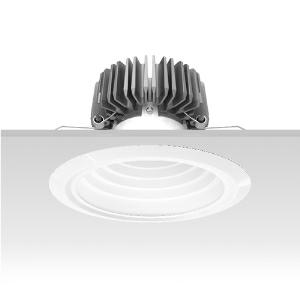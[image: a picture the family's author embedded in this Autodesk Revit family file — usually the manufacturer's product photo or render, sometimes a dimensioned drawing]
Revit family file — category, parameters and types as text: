
# Revit family: 3f_filippi_-_3f_reno_bianco_ampio_3f_filippi_-_30687_a01025_-_3f_reno_200_wh_4000-840_dali_wide___vt_wh_5cad
name_source: partatom
category: Lighting Fixtures
units: mm (PartAtom-declared; Revit-internal decimal feet)

## family parameters
Cut with Voids When Loaded = No
Host = Face
Light Source = No
Part Type = Normal
Room Calculation Point = No
Round Connector Dimension = Use Diameter
Shared = No

## types (1)
- 3F Filippi - 3F Reno Bianco Ampio (1 x LED, 3379 lm, 36 W, 4000 K)
    Apparent Load = 36 VA
    Approval mark = CE
    CIE Flux Codes = 75 94 99 100 100
    Color Rendering = 80
    Color Temperature = 4000 K
    Control Gear = Electronic transformer
    Default Elevation = 1800 mm
    Description = ILLUMINOTECHNICAL
Luminous efficiency 100% (DLOR 100%, ULOR 0%).
Initial luminous flux of the luminaire 3379 lm.
Direct symmetric wide distribution.
Installation Interdistance Transv.D = 1.56 x hu - Long.D = 1.56 x hu.
Tabular UGR (CIE 117 - 4H-8H; S=0.25H; 70/50/20): RUG 22.8 - 22.7.
Beam angle: 74° - 74°.
Luminous efficacy 94 lm/W.
Lifetime (L90/B10): 30000 h. (tq+25°C)
Lifetime (L85/B10): 50000 h. (tq+25°C)
Lifetime (L70/B10): 80000 h. (tq+25°C)
Sudden decreased luminous flux after 50000 hours: 0% (C0).
Photobiological safety in compliance with IEC/TR 62778: RG1 low risk, (IEC 62471).
In compliance with IEC/EN 62722-2-1 - IEC/EN 62717 standards.

SOURCE
Compact LED module 4000/840.
Energy efficiency class (UE 2019/2020 - UE 2019/2015): D.
CIE 13.3 Colour rendering index: CRI >80 (R9 <50%).
IES TM-30 Fidelity Index: Rf = 84 Rg = 95.
CCT nominal colour temperature 4000 K.
Colour initial tolerance (MacAdam): SDCM 3.
Zhaga Book 3 compliant.

MECHANICAL
Passive heat dissipator in die-casting aluminium, oversized, for optimum thermal management of the LED module.
Parabolic element with graduated/concentric rings in white polycarbonate.
Transparent external lens with glossy and satin differentiated surfaces, with a cooling and anti-insect system in methacrylate (PMMA).
Fastening spring clips in stainless steel.
Dimensions: diameter 226 mm, height 146 mm. Weight 1.76 kg.
IP44 protection degree for exposed part, IP20 for recessed part.
Mechanical strength to impacts IK06 (1 joule).
Glow-wire test resistance 650°C.

ELECTRICAL
Wiring on a separate unit.
Halogen Free DALI-2 DATI (Parts 251, 252, 253), PUSH-DIM, electronic wiring 230V-50/60Hz, power factor 0.97 at full load, THD <25%, constant output current, SELV, class II, 1 driver, 1 DALI addresse.
Power of the luminaire 36 W.
ENEC - CE.
SAFE FLICKER: PstLM=<1 and SVM=<0.4 (IEC TR 61547-1 and IEC TR 63158), to ensure a more comfortable and safe light.
Luminaire compliant with EN 60598-2-22 for power supply from a centralised emergency system CPSS (Central Power Supply System), not incorporated in the luminaire - high risk areas excluded. The default power and flux are 100% in AC and 100% in DC.
Ambient temperature from 0°C to +25°C.
Temperature class T6 max 85°C.
Relative humidity UR: <85%.

INSTALLATION
Pull-up recessed fitting.
False ceiling carving: 200 mm.
All accessories dedicated to this product are available on the Catalog and on our website www.3F-Filippi.com.

ACCESSORIES
A01025 - VT transparent glass, tempered, not flammable, locked and in line with the trim, in white polycarbonate.

APPLICATIONS
Environments: architectural, commercial, exhibition areas, transit areas, corridors, shops, display windows, service areas.
In false ceilings with narrow voids.

LIGHT MANAGEMENT
Recommended minimum setting: 10%.
The luminaire, equipped with (DALI-2 DATI) driver, can be controlled manually with 3F Easy Dim technology or automatically/manually with wired or wireless DALI/D2D control systems.
The D2D driver guarantees interoperability with other devices with the same certification by making the following information available:
Device Data (Part 251), Energy Report (Part 252), Diagnosis & Maintenance (Part 253).
In electrical systems without a regulation system (manual or automatic) and DALI bus, a suitable jumper must be made on the DA-DA terminals of the appliance.

WARNING
Luminaire designed for disposal/recycling at end-of-life.
Replaceable (LED only) light source by a professional. Replaceable control gear by a professional.
    Height = 0 mm  [stored 0 ft]
    Lamp = 1 x LED
    Lamp Light Flux = 3379 lm
    Lamp Power = 36 W
    Lamp count = 1
    Length = 226 mm
    Lifetime = 50000 h
    Luminous efficacy = 94 lm/W
    Manufacturer = 3F Filippi
    ModVariant = No
    Model = 3F Filippi - 30687+A01025 - 3F Reno 200 WH 4000-840 DALI WIDE + VT WH
    Mounting Place = Ceiling
    Mounting Type = Recessed
    Number of Poles = 1
    OnlyDefault = Yes
    Power Factor = 1
    Product Name = 3F Filippi - 3F Reno Bianco Ampio
    Product group = recessed luminaire
    ProductGroupID = 4
    Protection Class = Protection class II
    Protection Degree = IP 20
    RLX_Detail_Level = 1
    RLX_Emergency_Light_Flux = 0 lm
    RLX_Emergency_Type = 0
    RLX_Emergency_Type_DB = No
    RlxData = <blob elided: 97925 chars, md5=6a830136>
    Socket = socket
    Standby Power = 0 W
    System Light Flux = 3379 lm
    System Power = 36 W
    Type Comments = Product without accessories
    Type Image = 3ffilippi_3f_reno_200_wh__a01025.jpg
    URL = http://relux.com
    VarID = ---
    Voltage = 0 V
    Weight = 0.00 kg
    Width = 0 mm  [stored 0 ft]

note: [stored X ft] marks values corroborated as IEEE doubles in the binary element streams (Revit-internal decimal feet)

## geometry (parser evidence)
native form markers: Blend x4, Sweep x9
no freeform markers — native parametric forms only
